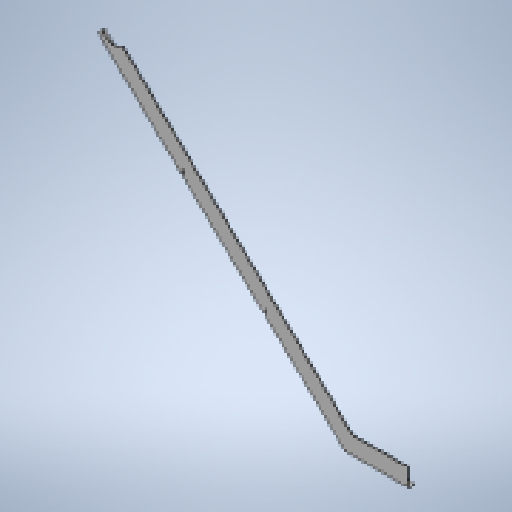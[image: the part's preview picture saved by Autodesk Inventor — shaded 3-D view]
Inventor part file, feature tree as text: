
AUTODESK INVENTOR PART (.ipt)
format: ipt  version: 2025 (Build 290162010, 162A)  size: 390,656 bytes
history: native  units: mm
features: other x6, sheet_metal_op x4, sketch x4, extrude x1, pattern_linear x1
ambient origin geometry x8: Origin, YZ Plane, XZ Plane, XY Plane, X Axis, Y Axis, Z Axis, Center Point
bodies: Body1 (feature_tree)
feature tree (16):
  sheet_metal_op  "Face1"
  sheet_metal_op  "Flange1"
  extrude  "Extrusion2"  Depth=2.75mm
  other  "A-Side Definition"
  pattern_linear  "Rectangular Pattern1"  Spacing1=1.0mm  [1 undecoded]
  other  "Corner Chamfer3"
  other  "Mark2"
  sketch  "Sketch2"  dims[d5=40.0mm d68=2.75mm d91=3.0mm]
  other  "Plate2"
  sketch  "Sketch3"  dims[d95=3.0mm]
  other  "Plate3"
  sheet_metal_op  "Bend2"
  sheet_metal_op  "Corner2"
  sketch  "Sketch5"  dims[d97=2.0mm]
  sketch  "Sketch7"  dims[d98=2.0mm d99=1.0mm d100=4.0mm d101=2.75mm d102=20.0mm d103=90.0deg d104=2.75mm d105=8.0mm d106=0.5mm d107=2.75mm d108=25.0mm d114=30.0mm d115=32.0mm d117=50.0mm d135=12.0mm d139=2.1mm d140=31.0mm d141=5.0mm d142=21.0mm d144=0.0mm d145=0.0mm d146=300.0mm d150=20.0mm d152=300.0mm d153=6.0mm d154=6.0mm d155=45.0deg d156=50.0mm d157=23.736478mm d158=900.0mm d159=140.0mm d160=30.0mm d162=15.0mm]
  other  "Definition1"
note: 1 required parameter value undecoded (feature->parameter linkage not recoverable at this tier; creation-order binding heuristic only, values carry confidence <= 0.55)
